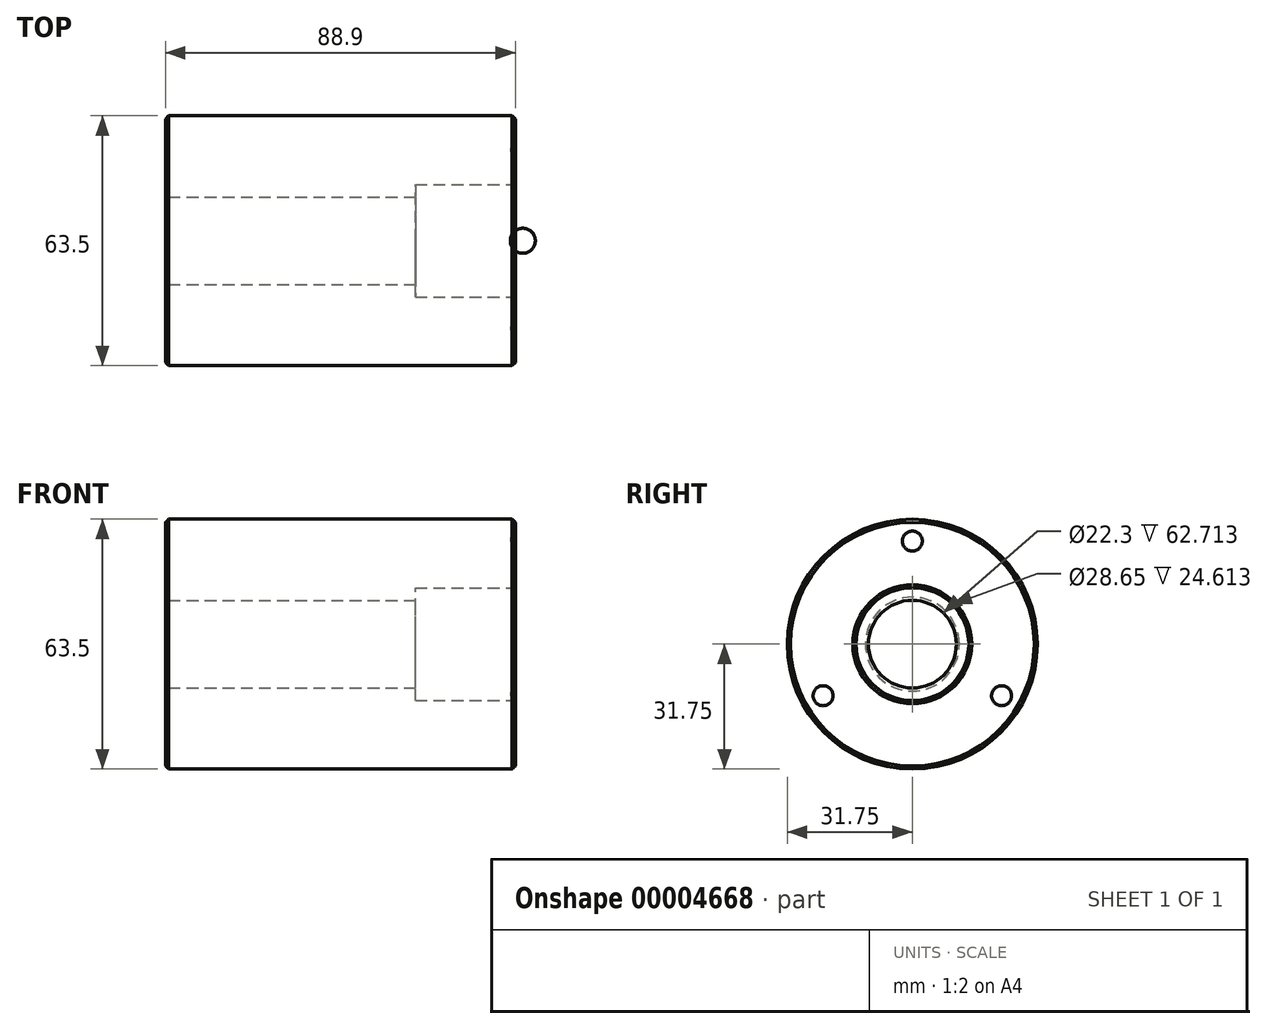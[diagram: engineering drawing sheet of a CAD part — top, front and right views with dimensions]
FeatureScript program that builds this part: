
annotation { "Feature Type Name" : "Feature", "Feature Type Description" : "" }
export const myFeature = defineFeature(function(context is Context, id is Id, definition is map)
    precondition{}
    {
        {
            var Q0;
            Q0=qCreatedBy(makeId("Front.planeOp"),FACE);
            var sketch = newSketch(context, id + "F0", { "sketchPlane" : qUnion([Q0])});
            skLineSegment(sketch, "E0", {"start": v(0, 31.75) * mm, "end": v(-88.9, 31.75) * mm});
            skLineSegment(sketch, "E1", {"start": v(-88.9, 31.75) * mm, "end": v(-88.9, 11.15) * mm});
            skLineSegment(sketch, "E2", {"start": v(-88.9, 11.15) * mm, "end": v(-25.4, 11.15) * mm});
            skLineSegment(sketch, "E3", {"start": v(-25.4, 11.15) * mm, "end": v(-25.4, 14.33) * mm});
            skLineSegment(sketch, "E4", {"start": v(-25.4, 14.33) * mm, "end": v(0, 14.33) * mm});
            skLineSegment(sketch, "E5", {"start": v(0, 14.33) * mm, "end": v(0, 31.75) * mm});
            skLineSegment(sketch, "E6", {"start": v(11.3, 0) * mm, "end": v(-95.78, 0) * mm, "construction": true});
            skSolve(sketch);
        }
        {
            var Q0;
            Q0=makeQuery(id+"F0.imprint","IMPRINT",FACE,{"disambiguationData":[TD([[makeQuery(id+"F0.imprint","IMPRINT",EDGE,{"derivedFrom":sQuery(id+"F0.wireOp",EDGE,"E0")}),1.0]])]});
            var Q1;
            Q1=sQuery(id+"F0.wireOp",EDGE,"E6");
            revolve(context, id + "F1", {"entities" : qUnion([Q0]), "axis" : qUnion([Q1]), "revolveType" : RevolveType.FULL});
        }
        {
            var Q0;
            Q0=qCreatedBy(makeId("Front.planeOp"),FACE);
            var sketch = newSketch(context, id + "F2", { "sketchPlane" : qUnion([Q0])});
            skArc(sketch, "E7", {"start": v(1.9, 29.36) * mm, "mid": v(-1.27, 26.19) * mm, "end": v(1.9, 23.01) * mm});
            skLineSegment(sketch, "E8", {"start": v(1.9, 23.01) * mm, "end": v(1.9, 29.36) * mm});
            skSolve(sketch);
        }
        {
            var Q0;
            Q0 = qSketchRegion(id + "F2", true);
            var Q1;
            Q1=sQuery(id+"F2.wireOp",EDGE,"E8");
            revolve(context, id + "F3", {"operationType" : NewBodyOperationType.REMOVE, "entities" : qUnion([Q0]), "axis" : qUnion([Q1]), "revolveType" : RevolveType.FULL, "oppositeDirection" : true});
        }
        {
            var Q0;
            Q0=makeQuery(id+"F3.boolean.opBoolean","COPY",FACE,{"derivedFrom":makeQuery(id+"F3.opRevolve","SWEPT_FACE",FACE,{"disambiguationData":[OSD([sQuery(id+"F2.wireOp",EDGE,"E7")])]})});
            var Q1;
            Q1=makeQuery(id+"F1.opRevolve","SWEPT_FACE",FACE,{"disambiguationData":[OSD([sQuery(id+"F0.wireOp",EDGE,"E4")])]});
            circularPattern(context, id + "F4", {"faces" : qUnion([Q0]), "axis" : qUnion([Q1]), "angle" : 120 * degree, "instanceCount" : 3, "patternType" : PatternType.FACE});
        }
        {
            var Q0;
            Q0=makeQuery(id+"F1.opRevolve","SWEPT_EDGE",EDGE,{"disambiguationData":[OSD([sQuery(id+"F0.wireOp",EDGE,"E0"),sQuery(id+"F0.wireOp",EDGE,"E5")])]});
            var Q1;
            Q1=makeQuery(id+"F1.opRevolve","SWEPT_EDGE",EDGE,{"disambiguationData":[OSD([sQuery(id+"F0.wireOp",EDGE,"E4"),sQuery(id+"F0.wireOp",EDGE,"E5")])]});
            var Q2;
            Q2=makeQuery(id+"F1.opRevolve","SWEPT_FACE",FACE,{"disambiguationData":[OSD([sQuery(id+"F0.wireOp",EDGE,"E1")])]});
            chamfer(context, id + "F5", {"entities" : qUnion([Q0, Q1, Q2]), "width" : 0.79 * mm, "tangentPropagation" : true});
        }
    });
